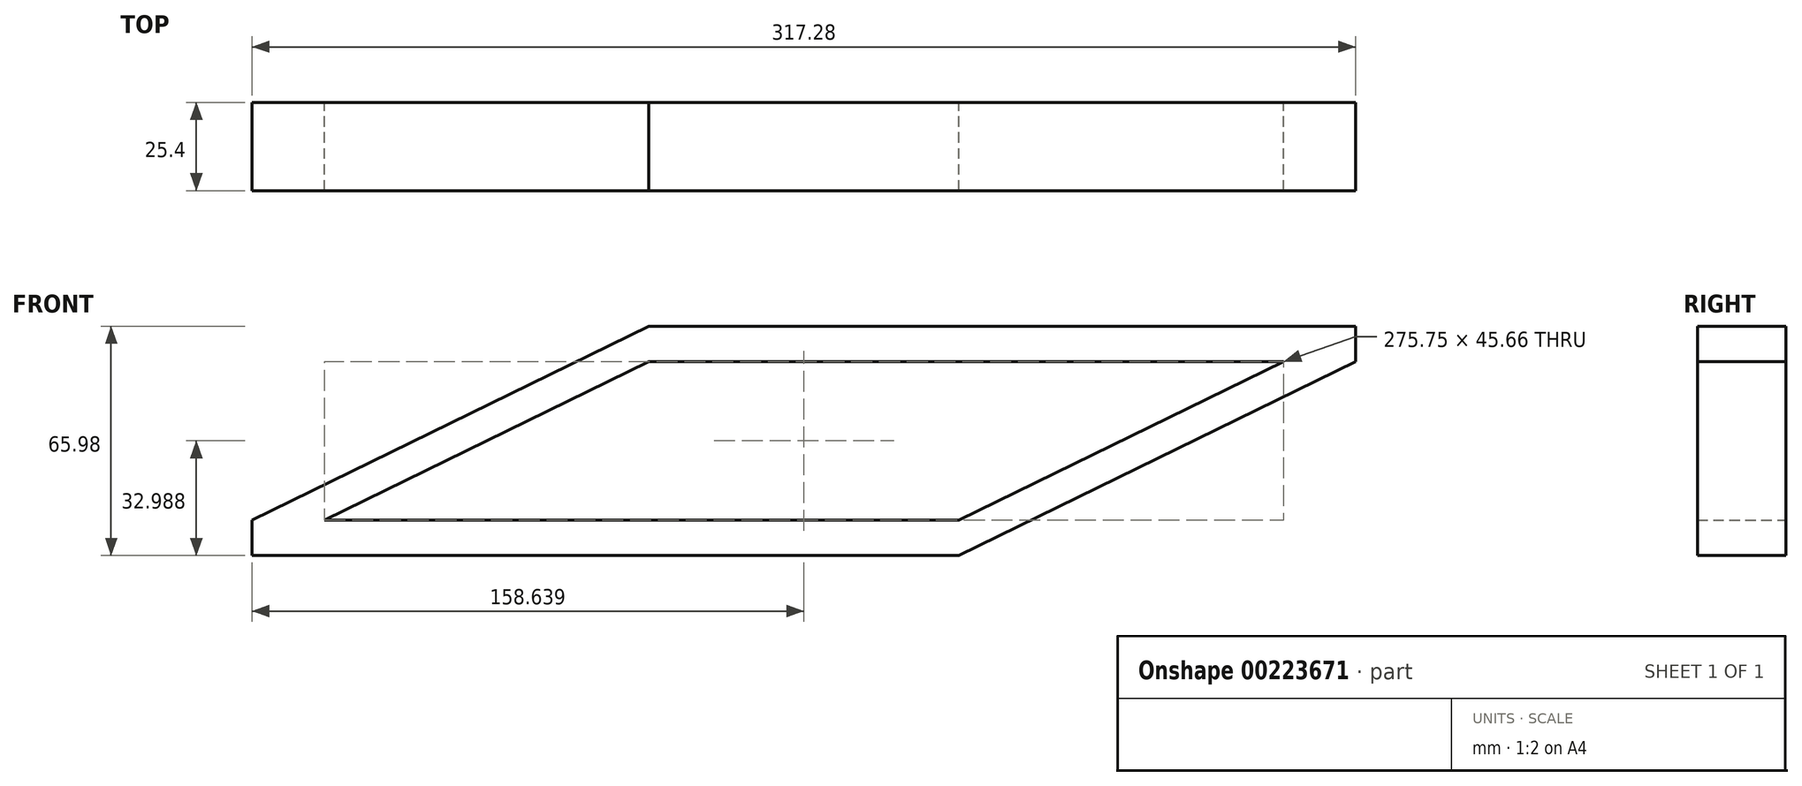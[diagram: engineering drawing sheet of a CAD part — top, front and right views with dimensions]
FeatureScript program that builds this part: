
annotation { "Feature Type Name" : "Feature", "Feature Type Description" : "" }
export const myFeature = defineFeature(function(context is Context, id is Id, definition is map)
    precondition{}
    {
        {
            var Q0;
            Q0=qCreatedBy(makeId("Front.planeOp"),FACE);
            var sketch = newSketch(context, id + "F0", { "sketchPlane" : qUnion([Q0])});
            skLineSegment(sketch, "E0.bottom", {"start": v(101.6, -5.08) * mm, "end": v(-101.6, -5.08) * mm});
            skLineSegment(sketch, "E0.top", {"start": v(101.6, 5.08) * mm, "end": v(-101.6, 5.08) * mm});
            skLineSegment(sketch, "E0.left", {"start": v(101.6, -5.08) * mm, "end": v(101.6, 5.08) * mm});
            skLineSegment(sketch, "E0.right", {"start": v(-101.6, -5.08) * mm, "end": v(-101.6, 5.08) * mm});
            skPoint(sketch, "E0.middle", {"position": v(0, 0) * mm});
            skLineSegment(sketch, "E1.bottom", {"start": v(215.68, 60.9) * mm, "end": v(12.48, 60.9) * mm});
            skLineSegment(sketch, "E1.top", {"start": v(215.68, 50.74) * mm, "end": v(12.48, 50.74) * mm});
            skLineSegment(sketch, "E1.left", {"start": v(215.68, 60.9) * mm, "end": v(215.68, 50.74) * mm});
            skLineSegment(sketch, "E1.right", {"start": v(12.48, 60.9) * mm, "end": v(12.48, 50.74) * mm});
            skPoint(sketch, "E1.middle", {"position": v(114.08, 55.82) * mm});
            skLineSegment(sketch, "E2", {"start": v(-101.6, 5.08) * mm, "end": v(12.48, 60.9) * mm});
            skLineSegment(sketch, "E3", {"start": v(101.6, 5.08) * mm, "end": v(215.68, 60.9) * mm});
            skLineSegment(sketch, "E4", {"start": v(101.6, -5.08) * mm, "end": v(215.68, 50.74) * mm});
            skLineSegment(sketch, "E5", {"start": v(-101.6, -5.08) * mm, "end": v(12.48, 50.74) * mm});
            skSolve(sketch);
        }
        {
            var Q0;
            Q0 = qSketchRegion(id + "F0", true);
            extrude(context, id + "F1", {"entities" : qUnion([Q0]), "depth" : 25.4 * mm});
        }
    });
